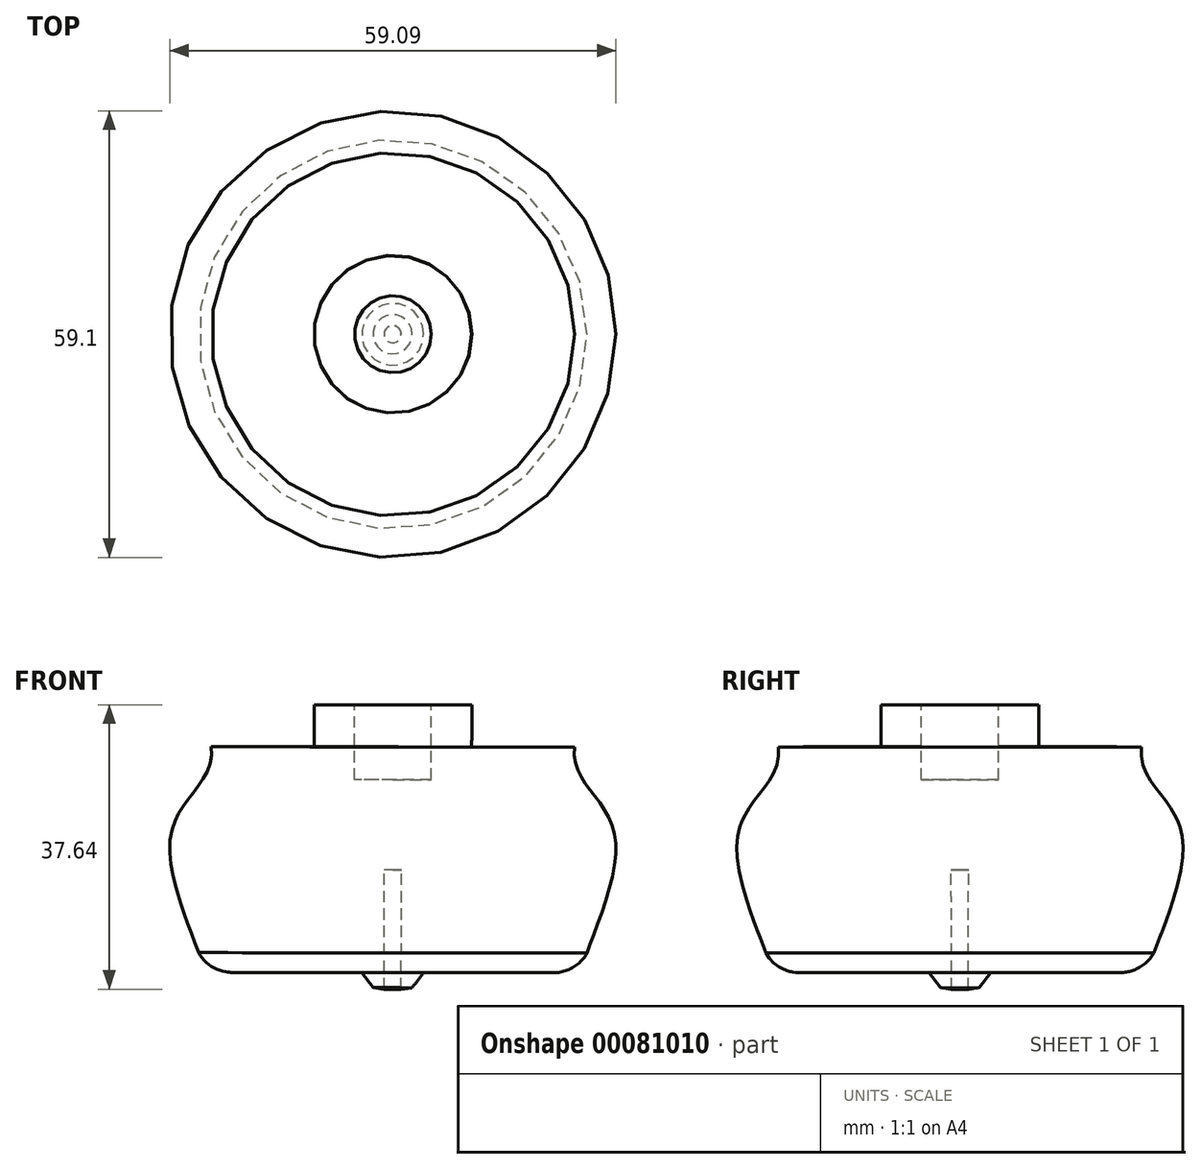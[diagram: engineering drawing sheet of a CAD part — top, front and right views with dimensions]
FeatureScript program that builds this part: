
annotation { "Feature Type Name" : "Feature", "Feature Type Description" : "" }
export const myFeature = defineFeature(function(context is Context, id is Id, definition is map)
    precondition{}
    {
        {
            var Q0;
            Q0=qCreatedBy(makeId("Front.planeOp"),FACE);
            var sketch = newSketch(context, id + "F0", { "sketchPlane" : qUnion([Q0])});
            skLineSegment(sketch, "E0", {"start": v(-5.38, 5.55) * mm, "end": v(-10.73, 5.55) * mm});
            skLineSegment(sketch, "E1", {"start": v(-10.73, 5.55) * mm, "end": v(-10.73, 0) * mm});
            skLineSegment(sketch, "E2", {"start": v(-10.73, 0) * mm, "end": v(-24.34, 0) * mm});
            skLineSegment(sketch, "E3", {"start": v(-21.6, -29.87) * mm, "end": v(-4.43, -29.87) * mm});
            skLineSegment(sketch, "E4", {"start": v(-0.3, -4.4) * mm, "end": v(-5.38, -4.35) * mm});
            skLineSegment(sketch, "E5", {"start": v(-5.38, -4.35) * mm, "end": v(-5.38, 5.55) * mm});
            skPoint(sketch, "E6.orphan", {"position": v(0, 5.55) * mm});
            skPoint(sketch, "E7.end.orphan", {"position": v(0, -32.29) * mm});
            skLineSegment(sketch, "E8", {"start": v(-4.43, -29.87) * mm, "end": v(-2.93, -31.89) * mm});
            skLineSegment(sketch, "E9", {"start": v(-2.93, -31.89) * mm, "end": v(-1.46, -32.09) * mm});
            skLineSegment(sketch, "E10", {"start": v(-1.46, -32.09) * mm, "end": v(-1.46, -15.04) * mm});
            skPoint(sketch, "E10.endSnap0", {"position": v(-1.46, -32.09) * mm});
            skLineSegment(sketch, "E11", {"start": v(-1.8, -16.3) * mm, "end": v(-0.32, -16.3) * mm});
            skFitSpline(sketch, "E12", {"points": [v(-24.34, 0) * mm, v(-29.82, -12.45) * mm, v(-25.6, -29.87) * mm], "startDerivative": vector(4.1, -31.39) * mm, "endDerivative": vector(-7.59, 0) * mm});
            skLineSegment(sketch, "E13", {"start": v(-0.3, -4.4) * mm, "end": v(-0.32, -16.3) * mm});
            skArc(sketch, "E14", {"start": v(-26.04, -27.25) * mm, "mid": v(-24.18, -29.16) * mm, "end": v(-21.6, -29.87) * mm});
            skSolve(sketch);
        }
        {
            var Q0;
            Q0=makeQuery(id+"F0.imprint","IMPRINT",FACE,{"disambiguationData":[TD([[makeQuery(id+"F0.imprint","IMPRINT",EDGE,{"derivedFrom":sQuery(id+"F0.wireOp",EDGE,"E0")}),1.0]])]});
            var Q1;
            Q1=sQuery(id+"F0.wireOp",EDGE,"E13");
            revolve(context, id + "F1", {"entities" : qUnion([Q0]), "axis" : qUnion([Q1]), "revolveType" : RevolveType.FULL});
        }
    });
